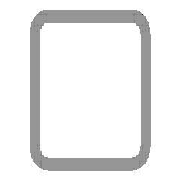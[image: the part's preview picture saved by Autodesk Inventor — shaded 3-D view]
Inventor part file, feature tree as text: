
AUTODESK INVENTOR PART (.ipt)
format: ipt  version: 2022 (Build 260153000, 153)  size: 264,704 bytes
history: native  units: mm (DEFAULTED — no unit token found)
features: other x7, sketch x3, surface_op x2, plane x1
ambient origin geometry x8: Origin, YZ Plane, XZ Plane, XY Plane, X Axis, Y Axis, Z Axis, Center Point
bodies: Solid1 (feature_tree), Body (feature_tree), Solid3 (feature_tree)
feature tree (13):
  parser-record x1  (decoder bookkeeping rows leaked as tree rows — omitted from the tree; the rows remain in map.json)
  other  "Driven Length"
  other  "Start Plane"
  other  "End Plane"
  sketch  "Sketch"  dims[d7=6.0mm d10=40.0mm d11=40.0mm d12=4.0mm d13=-0.0mm d14=180.0mm d15=20.0mm d16=20.0mm d17=90.0deg d18=180.0mm d37=5.0mm d38=5.0mm d39=5.0mm d40=5.0mm d41=5.0mm d42=5.0mm d43=5.0mm d44=5.0mm d45=0.0mm d46=5.0mm d47=5.0mm d48=5.0mm d49=5.0mm d50=5.0mm d51=5.0mm d52=5.0mm d53=5.0mm d54=0.0mm]
  sketch  "Sketch3"  dims[d3=155.0mm]
  plane  "Work Plane3"
  sketch  "Sketch4"  dims[d4=0.0mm]
  other  "Srf5"
  other  "Srf6"
  other  "Srf4"
  surface_op  "Boundary Patch3"
  surface_op  "Boundary Patch4"
